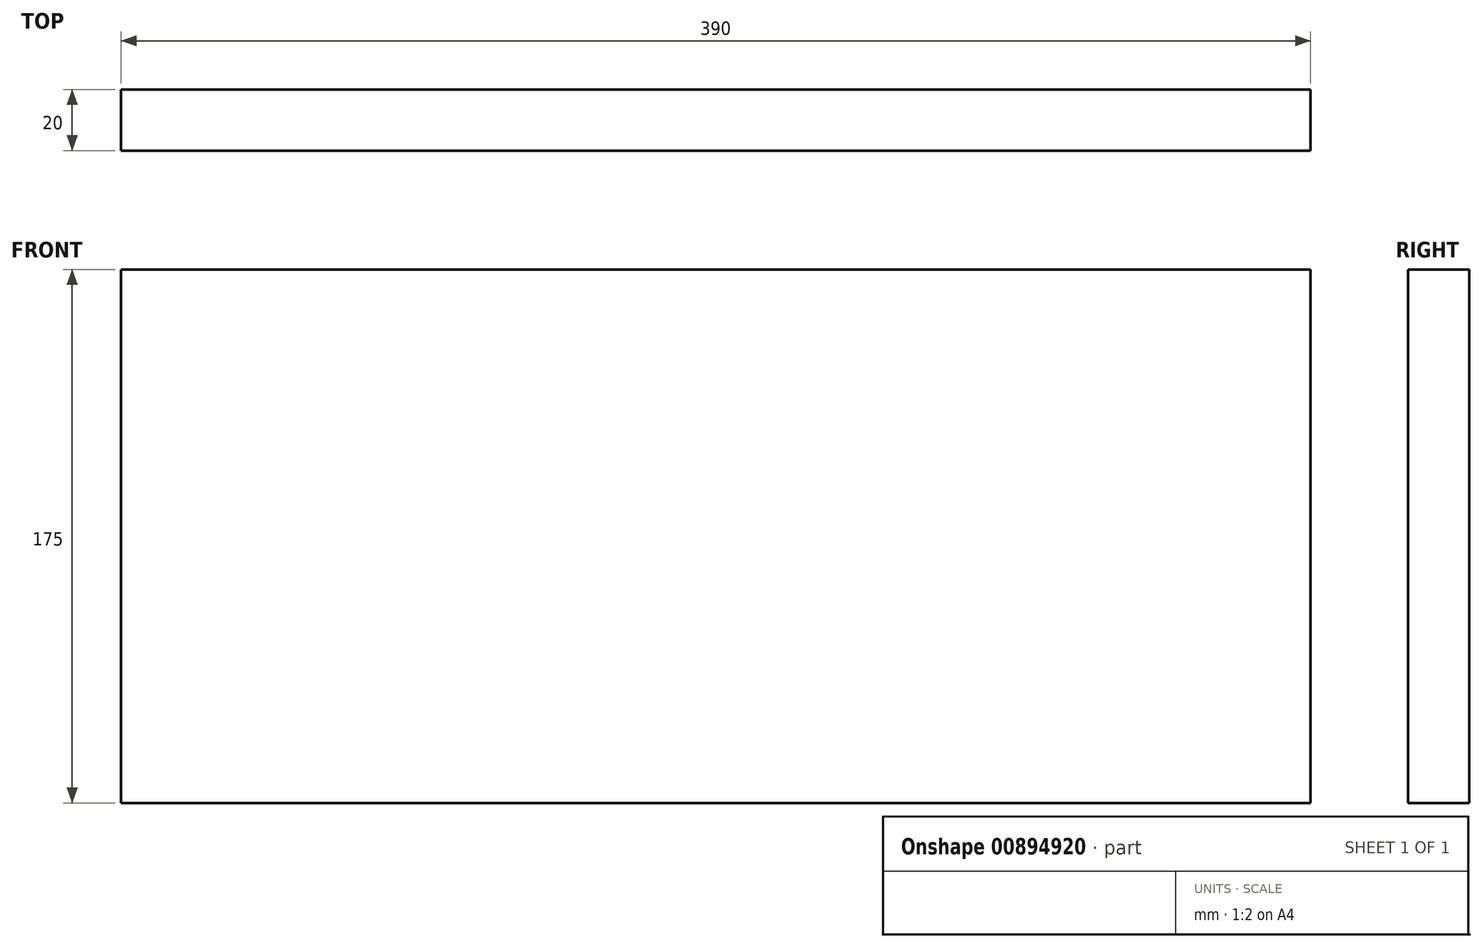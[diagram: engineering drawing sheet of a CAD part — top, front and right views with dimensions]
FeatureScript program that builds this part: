
annotation { "Feature Type Name" : "Feature", "Feature Type Description" : "" }
export const myFeature = defineFeature(function(context is Context, id is Id, definition is map)
    precondition{}
    {
        {
            var Q0;
            Q0=qCreatedBy(makeId("Front.planeOp"),FACE);
            var sketch = newSketch(context, id + "F0", { "sketchPlane" : qUnion([Q0])});
            skLineSegment(sketch, "E0.bottom", {"start": v(0, 0) * mm, "end": v(390, 0) * mm});
            skLineSegment(sketch, "E0.top", {"start": v(0, -175) * mm, "end": v(390, -175) * mm});
            skLineSegment(sketch, "E0.left", {"start": v(0, 0) * mm, "end": v(0, -175) * mm});
            skLineSegment(sketch, "E0.right", {"start": v(390, 0) * mm, "end": v(390, -175) * mm});
            skSolve(sketch);
        }
        {
            var Q0;
            Q0=makeQuery(id+"F0.imprint","IMPRINT",FACE,{"disambiguationData":[TD([[makeQuery(id+"F0.imprint","IMPRINT",EDGE,{"derivedFrom":sQuery(id+"F0.wireOp",EDGE,"E0.bottom")}),-1.0]])]});
            extrude(context, id + "F1", {"entities" : qUnion([Q0]), "depth" : 20 * mm, "offsetDistance" : 25 * mm});
        }
    });
